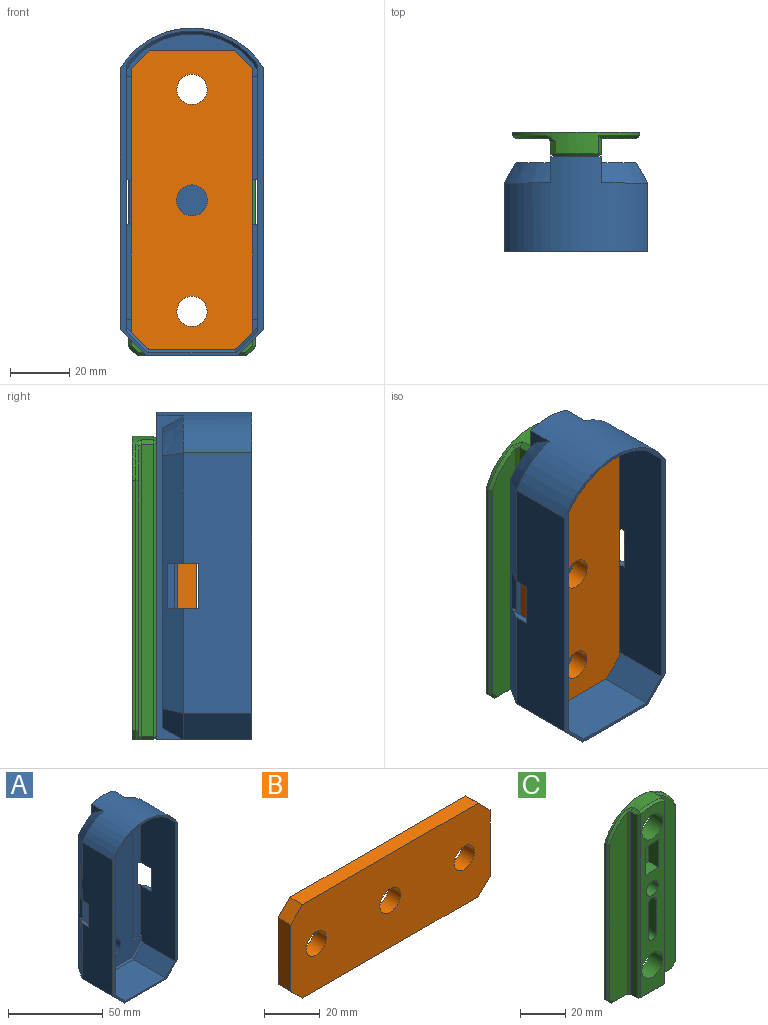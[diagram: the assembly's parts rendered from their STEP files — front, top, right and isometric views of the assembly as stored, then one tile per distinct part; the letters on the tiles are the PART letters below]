
ASSEMBLY  parts=3 mates=5
PART A: 50 faces, bbox 48.5x32x110.8 mm
  f0: cylinder r=27.29mm len=44.5mm, axis (0,1,0), area 1248.8mm2, adj f1,f5,f9,f46
  f1: plane 90.04x26.04mm, normal (1,0,0), area 2210.4mm2, adj f0,f2,f6,f9,f20,f22,f26,f29
  f2: plane 24x7.25mm, normal (0.71,0,0.71), area 246.1mm2, adj f1,f3,f9,f49
  f3: plane 30x24mm, normal (0,0,1), area 720mm2, adj f2,f4,f9,f48
  f4: plane 24x7.25mm, normal (-0.71,0,0.71), area 246.1mm2, adj f3,f5,f9,f47
  f5: plane 90.04x26.04mm, normal (-1,0,0), area 2210.4mm2, adj f0,f4,f7,f9,f23,f25,f26,f33
  f6: plane 82x7.25mm, normal (0,-1,0), area 579.5mm2, adj f1,f20,f21,f22,f29,f31,f32
  f7: plane 82x7.25mm, normal (0,-1,0), area 564.5mm2, adj f5,f23,f24,f25,f33,f35,f36
  f8: plane 101.2x11.75mm, normal (0,1,0), area 1125.1mm2, adj f18,f42,f43,f44,f45
  f9: plane 110.74x48.5mm, normal (0,-1,0), area 464.7mm2, adj f0,f1,f2,f3,f4,f5,f11,f12
  f10: plane 101.2x11.75mm, normal (0,1,0), area 1125.1mm2, adj f17,f36,f37,f38,f39,f40,f41
  f11: cylinder r=28.29mm len=48.5mm, axis (0,1,0), area 1498.5mm2, adj f9,f12,f16,f17,f18,f19,f40,f45
  f12: plane 88.18x23.07mm, normal (-1,0,0), area 1958.4mm2, adj f9,f11,f13,f29,f30,f31,f44
  f13: plane 23.07x8.84mm, normal (-0.71,0,-0.71), area 288.3mm2, adj f9,f12,f14,f43
  f14: plane 32x30.83mm, normal (0,0,-1), area 863mm2, adj f9,f13,f15,f17,f18,f19,f39,f42
  f15: plane 23.07x8.84mm, normal (0.71,0,-0.71), area 288.3mm2, adj f9,f14,f16,f38
  f16: plane 88.18x23.07mm, normal (1,0,0), area 1958.4mm2, adj f9,f11,f15,f33,f34,f35,f37,f41
  f17: plane 109.43x8.93mm, normal (1,0,0), area 247.3mm2, adj f10,f11,f14,f19,f39,f40
  f18: plane 109.43x8.93mm, normal (-1,0,0), area 247.3mm2, adj f8,f11,f14,f19,f42,f45
  f19: plane 110.74x17mm, normal (0,1,0), area 1609.8mm2, adj f11,f14,f17,f18,f27,f28
  f20: plane 7.25x1mm, normal (0,0,-1), area 7.2mm2, adj f1,f6,f21,f26
  f21: plane 82x1mm, normal (-1,0,0), area 82mm2, adj f6,f20,f22,f26
  f22: plane 7.25x1mm, normal (0,0,1), area 7.2mm2, adj f1,f6,f21,f26
  f23: plane 7.25x1mm, normal (0,0,1), area 7.2mm2, adj f5,f7,f24,f26
  f24: plane 82x1mm, normal (1,0,0), area 82mm2, adj f7,f23,f25,f26
  f25: plane 7.25x1mm, normal (0,0,-1), area 7.2mm2, adj f5,f7,f24,f26
  f26: plane 106.74x44.5mm, normal (0,-1,0), area 3075.8mm2, adj f1,f5,f20,f21,f22,f23,f24,f25
  f27: cylinder r=6.5mm len=13mm, axis (0,1,0), area 285.9mm2, adj f19,f26
  f28: cylinder r=6.5mm len=13mm, axis (0,1,0), area 285.9mm2, adj f19,f26
  f29: plane 10.27x3mm, normal (0,0,-1), area 15mm2, adj f1,f6,f12,f30,f32,f44
  f30: plane 15x2mm, normal (0,1,0), area 30mm2, adj f1,f12,f29,f31
  f31: plane 10.27x3mm, normal (0,0,1), area 15mm2, adj f1,f6,f12,f30,f32,f44
  f32: plane 15x2.27mm, normal (-1,0,0), area 34mm2, adj f6,f29,f31,f44
  f33: plane 12x4mm, normal (0,0,1), area 18.1mm2, adj f5,f7,f16,f34,f36,f37
  f34: plane 15x2mm, normal (0,1,0), area 30mm2, adj f5,f16,f33,f35
  f35: plane 12x4mm, normal (0,0,-1), area 18.1mm2, adj f5,f7,f16,f34,f36,f41
  f36: plane 15x4mm, normal (1,0,0), area 60mm2, adj f7,f10,f33,f35
  f37: plane 35.68x6.93mm, normal (0.87,0.5,0), area 278.8mm2, adj f10,f16,f33,f38
  f38: plane 10.49x10.49mm, normal (0.61,0.5,-0.61), area 86.7mm2, adj f10,f15,f37,f39
  f39: plane 6.93x6.91mm, normal (0,0.5,-0.87), area 48.7mm2, adj f10,f14,f17,f38
  f40: cone r=28.29mm half-angle=30deg, axis (0,-1,0), area 143mm2, adj f10,f11,f17,f41
  f41: plane 37.5x6.93mm, normal (0.87,0.5,0), area 295.4mm2, adj f10,f16,f35,f40
  f42: plane 6.93x6.91mm, normal (0,0.5,-0.87), area 48.7mm2, adj f8,f14,f18,f43
  f43: plane 10.49x10.49mm, normal (-0.61,0.5,-0.61), area 86.7mm2, adj f8,f13,f42,f44
  f44: plane 88.18x6.93mm, normal (-0.87,0.5,0), area 604.3mm2, adj f8,f12,f29,f31,f32,f43,f45
  f45: cone r=28.29mm half-angle=30deg, axis (0,-1,0), area 143mm2, adj f8,f11,f18,f44
  f46: cone r=26.29mm half-angle=45deg, axis (0,-1,0), area 74.3mm2, adj f0,f1,f5,f26
  f47: plane 8.66x7.66mm, normal (-0.5,-0.71,0.5), area 14.9mm2, adj f4,f5,f26,f48
  f48: plane 30x1mm, normal (0,-0.71,0.71), area 41.8mm2, adj f3,f26,f47,f49
  f49: plane 8.66x7.66mm, normal (0.5,-0.71,0.5), area 14.9mm2, adj f1,f2,f26,f48
PART B: 13 faces, bbox 101x6.4x41 mm
  f0: plane 101x41mm, normal (0,-1,0), area 3819mm2, adj f2,f3,f4,f5,f6,f7,f8,f9
  f1: plane 101x41mm, normal (0,1,0), area 3819mm2, adj f2,f3,f4,f5,f6,f7,f8,f9
  f2: plane 29x6.35mm, normal (-1,0,0), area 184.2mm2, adj f0,f1,f7,f9
  f3: plane 89x6.35mm, normal (0,0,-1), area 565.1mm2, adj f0,f1,f7,f8
  f4: plane 29x6.35mm, normal (1,0,0), area 184.2mm2, adj f0,f1,f8,f10
  f5: plane 89x6.35mm, normal (0,0,1), area 565.1mm2, adj f0,f1,f9,f10
  f6: cylinder r=5.25mm len=10.5mm, axis (0,1,0), area 209.5mm2, adj f0,f1
  f7: plane 6.35x6mm, normal (-0.71,0,-0.71), area 53.9mm2, adj f0,f1,f2,f3
  f8: plane 6.35x6mm, normal (0.71,0,-0.71), area 53.9mm2, adj f0,f1,f3,f4
  f9: plane 6.35x6mm, normal (-0.71,0,0.71), area 53.9mm2, adj f0,f1,f2,f5
  f10: plane 6.35x6mm, normal (0.71,0,0.71), area 53.9mm2, adj f0,f1,f4,f5
  f11: cylinder r=5.1mm len=10.2mm, axis (0,-1,0), area 203.5mm2, adj f0,f1
  f12: cylinder r=5.1mm len=10.2mm, axis (0,-1,0), area 203.5mm2, adj f0,f1
PART C: 49 faces, bbox 43x8.3x102.5 mm
  f0: plane 37x7.25mm, normal (0,0,-1), area 133.8mm2, adj f2,f4,f9,f26,f28,f30,f35,f36
  f1: plane 84.65x1.05mm, normal (-1,0,0), area 88.9mm2, adj f2,f4,f5,f29
  f2: plane 3x3mm, normal (-0.71,0,-0.71), area 4.5mm2, adj f0,f1,f4,f27
  f3: plane 100.5x15mm, normal (0,-1,0), area 961.7mm2, adj f7,f8,f14,f15,f16,f17,f19,f21
  f4: plane 102.5x43mm, normal (0,1,0), area 3958.4mm2, adj f0,f1,f2,f5,f6,f7,f8,f9
  f5: cylinder r=22.99mm len=43mm, axis (0,1,0), area 153.1mm2, adj f1,f4,f6,f32,f34,f39,f45,f46
  f6: plane 84.65x1.05mm, normal (1,0,0), area 88.9mm2, adj f4,f5,f9,f43
  f7: cylinder r=6.5mm len=13mm, axis (0,1,0), area 336.9mm2, adj f3,f4
  f8: cylinder r=6.5mm len=13mm, axis (0,1,0), area 336.9mm2, adj f3,f4
  f9: plane 3x3mm, normal (0.71,0,-0.71), area 4.5mm2, adj f0,f4,f6,f40
  f10: plane 98.08x5.2mm, normal (1,0,0), area 510mm2, adj f11,f36,f44,f48
  f11: plane 98.94x12.37mm, normal (0,-1,0), area 1129mm2, adj f10,f35,f40,f43,f46,f48
  f12: plane 98.87x4.2mm, normal (-1,0,0), area 415.3mm2, adj f30,f31,f38,f39
  f13: plane 98.34x11mm, normal (0,-1,0), area 1030.3mm2, adj f26,f27,f29,f31,f32
  f14: plane 15x6.2mm, normal (1,0,0), area 93mm2, adj f3,f15,f17,f18
  f15: plane 8x6.2mm, normal (0,0,-1), area 49.6mm2, adj f3,f14,f16,f18
  f16: plane 15x6.2mm, normal (-1,0,0), area 93mm2, adj f3,f15,f17,f18
  f17: plane 8x6.2mm, normal (0,0,1), area 49.6mm2, adj f3,f14,f16,f18
  f18: plane 15x8mm, normal (0,-1,0), area 120mm2, adj f14,f15,f16,f17
  f19: cylinder r=3.75mm len=7.5mm, axis (0,-1,0), area 146.1mm2, adj f3,f20
  f20: plane 7.5x7.5mm, normal (0,-1,0), area 44.2mm2, adj f19
  f21: cylinder r=2.5mm len=6.2mm, axis (0,-1,0), area 48.7mm2, adj f3,f22,f24,f25
  f22: plane 18x6.2mm, normal (-1,0,0), area 111.6mm2, adj f3,f21,f23,f25
  f23: cylinder r=2.5mm len=6.2mm, axis (0,-1,0), area 48.7mm2, adj f3,f22,f24,f25
  f24: plane 18x6.2mm, normal (1,0,0), area 111.6mm2, adj f3,f21,f23,f25
  f25: plane 23x5mm, normal (0,-1,0), area 109.6mm2, adj f21,f22,f23,f24
  f26: plane 9x1mm, normal (0,-0.71,-0.71), area 12.4mm2, adj f0,f13,f27,f28
  f27: plane 3.41x3.41mm, normal (-0.5,-0.71,-0.5), area 5.4mm2, adj f2,f13,f26,f29
  f28: plane 2x2mm, normal (-0.58,-0.58,-0.58), area 2.6mm2, adj f0,f26,f30,f31
  f29: plane 84.65x1mm, normal (-0.71,-0.71,0), area 119.3mm2, adj f1,f13,f27,f32
  f30: plane 4.2x1mm, normal (-0.71,0,-0.71), area 5.9mm2, adj f0,f12,f28,f33
  f31: plane 98.87x1mm, normal (-0.71,-0.71,0), area 139.5mm2, adj f12,f13,f28,f34
  f32: cone r=21.99mm half-angle=45deg, axis (0,1,0), area 24.1mm2, adj f5,f13,f29,f34
  f33: plane 1x1mm, normal (-0.58,-0.58,-0.58), area 0.9mm2, adj f30,f37,f38
  f34: bspline ~3.12x2.19mm, area 3.7mm2, adj f5,f31,f32,f39
  f35: plane 11x1mm, normal (0,-0.71,-0.71), area 14.6mm2, adj f0,f11,f36,f40
  f36: plane 6.2x1mm, normal (0.71,0,-0.71), area 8.1mm2, adj f0,f10,f35,f41
  f37: plane 15x1mm, normal (0,-0.71,-0.71), area 21.2mm2, adj f0,f3,f33,f41
  f38: plane 99.18x1mm, normal (-0.71,-0.71,0), area 140mm2, adj f3,f12,f33,f42
  f39: plane 4.2x1.56mm, normal (-0.71,0,0.71), area 9.2mm2, adj f5,f12,f34,f42
  f40: plane 3.41x3.41mm, normal (0.5,-0.71,-0.5), area 5.4mm2, adj f9,f11,f35,f43
  f41: plane 1x1mm, normal (0.58,-0.58,-0.58), area 0.9mm2, adj f36,f37,f44
  f42: plane 1.56x1.56mm, normal (-0.64,-0.44,0.64), area 1.2mm2, adj f38,f39,f45
  f43: plane 84.65x1mm, normal (0.71,-0.71,0), area 119.3mm2, adj f6,f11,f40,f46
  f44: plane 99.18x1mm, normal (0.71,-0.71,0), area 139.5mm2, adj f3,f10,f41,f47
  f45: cone r=21.99mm half-angle=45deg, axis (0,1,0), area 21.3mm2, adj f3,f5,f42,f47
  f46: cone r=21.99mm half-angle=45deg, axis (0,1,0), area 27mm2, adj f5,f11,f43,f48
  f47: plane 2.14x1.01mm, normal (0.83,-0.44,0.36), area 1.3mm2, adj f44,f45,f48
  f48: plane 6.2x2.13mm, normal (0.92,0,0.4), area 12.7mm2, adj f5,f10,f11,f46,f47
PLACE A t=(10.78,-46.37,52.81)mm
PLACE B rot(axis=(0,1,0),90deg) t=(10.78,-51.37,105.31)mm
PLACE C t=(10.78,-36.12,95.39)mm
MATE cylindrical C.f7 <-> A.f27  axis (0,1,0) through (10.78,-36.12,142.81)mm
MATE planar A.f26 <-> B.f6  axis (0,-1,0) through (-7.85,-51.37,65.06)mm
MATE cylindrical B.f12 <-> C.f7  axis (0,-1,0) through (10.78,-51.37,142.81)mm
MATE planar C.f3 <-> A.f19  axis (0,-1,0) through (6.78,-44.37,133.74)mm
MATE cylindrical B.f11 <-> C.f8  axis (0,1,0) through (10.78,-51.37,67.81)mm
